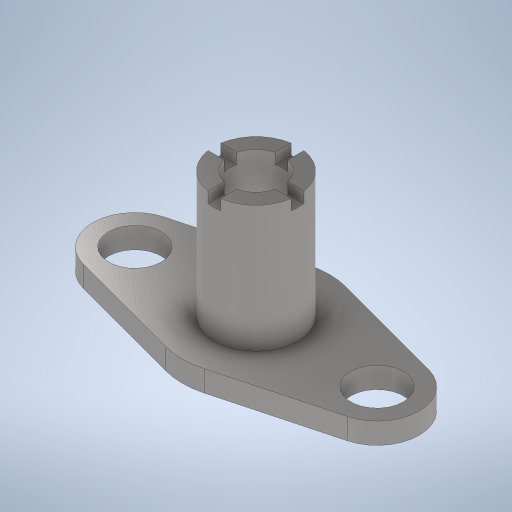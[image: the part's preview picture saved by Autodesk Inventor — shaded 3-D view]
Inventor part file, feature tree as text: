
AUTODESK INVENTOR PART (.ipt)
format: ipt  version: 2024 (Build 280153000, 153)  size: 335,360 bytes
history: native  units: mm
features: extrude x4, sketch x4, pattern_circular x1, fillet x1, projected_geometry x1
ambient origin geometry x8: Origin, YZ Plane, XZ Plane, XY Plane, X Axis, Y Axis, Z Axis, Center Point
bodies: Volumenkörper1 (feature_tree)
feature tree (11):
  extrude  "Extrusion1"  Depth=25.0mm
  extrude  "Extrusion2"  Depth=115.0mm
  extrude  "Extrusion3"  TaperAngle=30.0deg  [1 undecoded]
  extrude  "Extrusion4"  Depth=10.0mm TaperAngle=0.0deg
  pattern_circular  "Runde Anordnung1"  Count=4  [1 undecoded]
  fillet  "Rundung1"  Radius=60.0mm
  sketch  "Skizze1"  dims[d4=40.0mm d5=25.0mm]
  sketch  "Skizze2"  dims[d6=25.0mm d7=115.0mm]
  sketch  "Skizze3"  dims[d8=57.5mm d9=30.0deg]
  sketch  "Skizze4"  dims[d10=30.0deg d11=10.0mm d12=0.0mm d13=40.0mm d14=60.0mm d15=0.0mm d17=25.0mm d18=60.0mm d19=0.0mm d20=6.0mm d21=5.0mm d22=0.0mm d23=40.0mm d24=360.0deg d26=35.0mm]
  projected_geometry  "Projizierte Kontur1"
note: 2 required parameter values undecoded (feature->parameter linkage not recoverable at this tier; creation-order binding heuristic only, values carry confidence <= 0.55)
